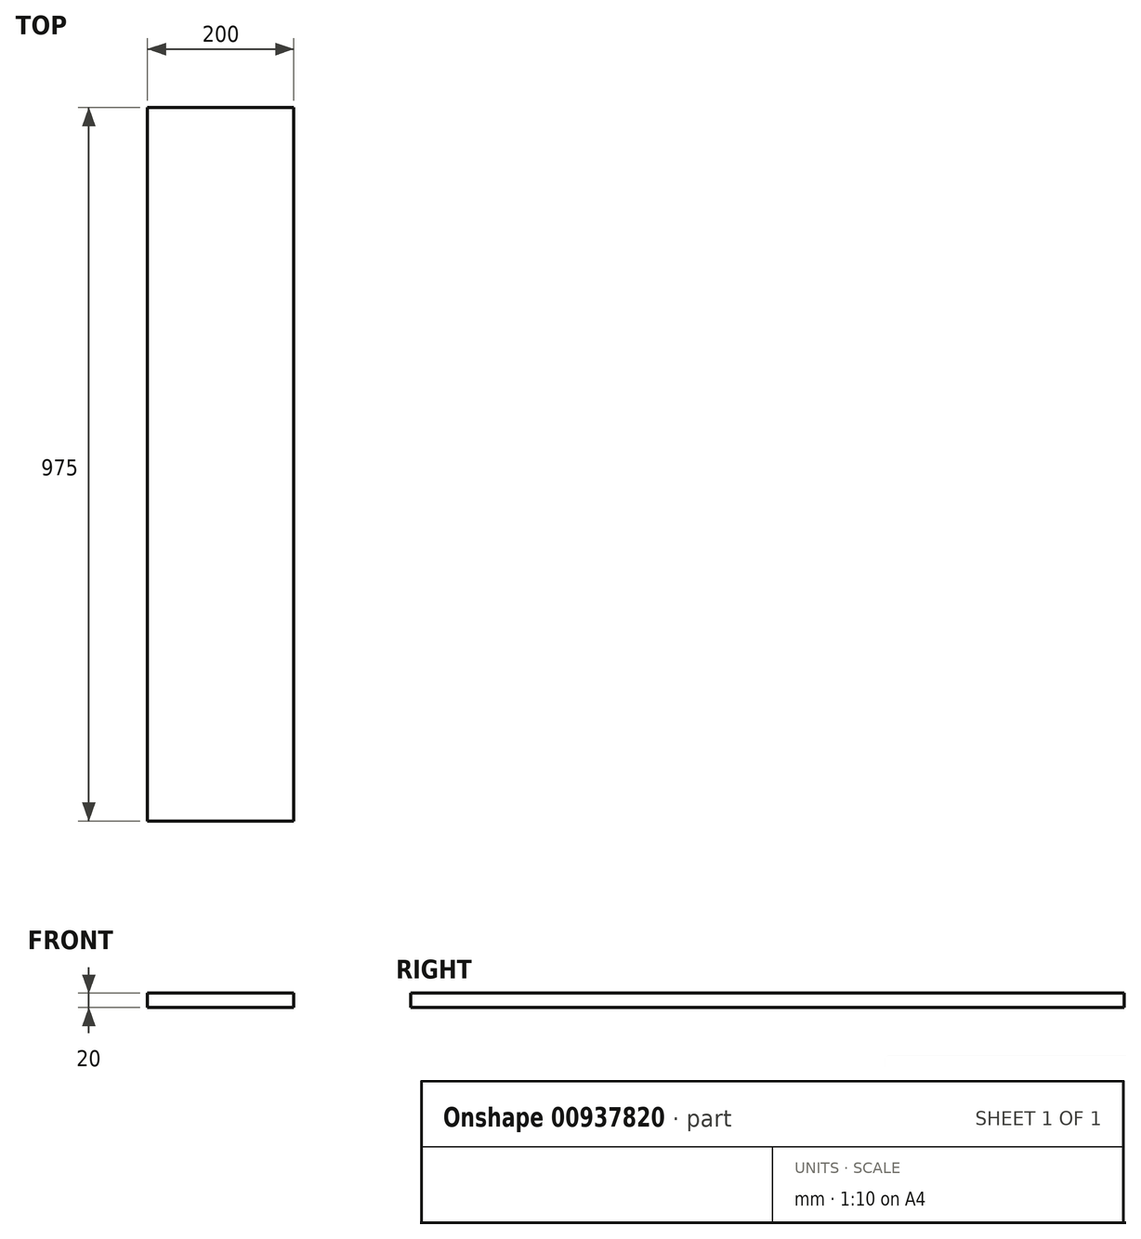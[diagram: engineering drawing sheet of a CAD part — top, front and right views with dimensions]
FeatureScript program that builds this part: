
annotation { "Feature Type Name" : "Feature", "Feature Type Description" : "" }
export const myFeature = defineFeature(function(context is Context, id is Id, definition is map)
    precondition{}
    {
        {
            var Q0;
            Q0=qCreatedBy(makeId("Front.planeOp"),FACE);
            var sketch = newSketch(context, id + "F0", { "sketchPlane" : qUnion([Q0])});
            skLineSegment(sketch, "E0.bottom", {"start": v(100, -10) * mm, "end": v(-100, -10) * mm});
            skLineSegment(sketch, "E0.top", {"start": v(100, 10) * mm, "end": v(-100, 10) * mm});
            skLineSegment(sketch, "E0.left", {"start": v(100, -10) * mm, "end": v(100, 10) * mm});
            skLineSegment(sketch, "E0.right", {"start": v(-100, -10) * mm, "end": v(-100, 10) * mm});
            skPoint(sketch, "E0.middle", {"position": v(0, 0) * mm});
            skSolve(sketch);
        }
        {
            var Q0;
            Q0=makeQuery(id+"F0.imprint","IMPRINT",FACE,{"disambiguationData":[TD([[makeQuery(id+"F0.imprint","IMPRINT",EDGE,{"derivedFrom":sQuery(id+"F0.wireOp",EDGE,"E0.bottom")}),-1.0]])]});
            extrude(context, id + "F1", {"entities" : qUnion([Q0]), "depth" : 975 * mm, "offsetDistance" : 25 * mm});
        }
    });
